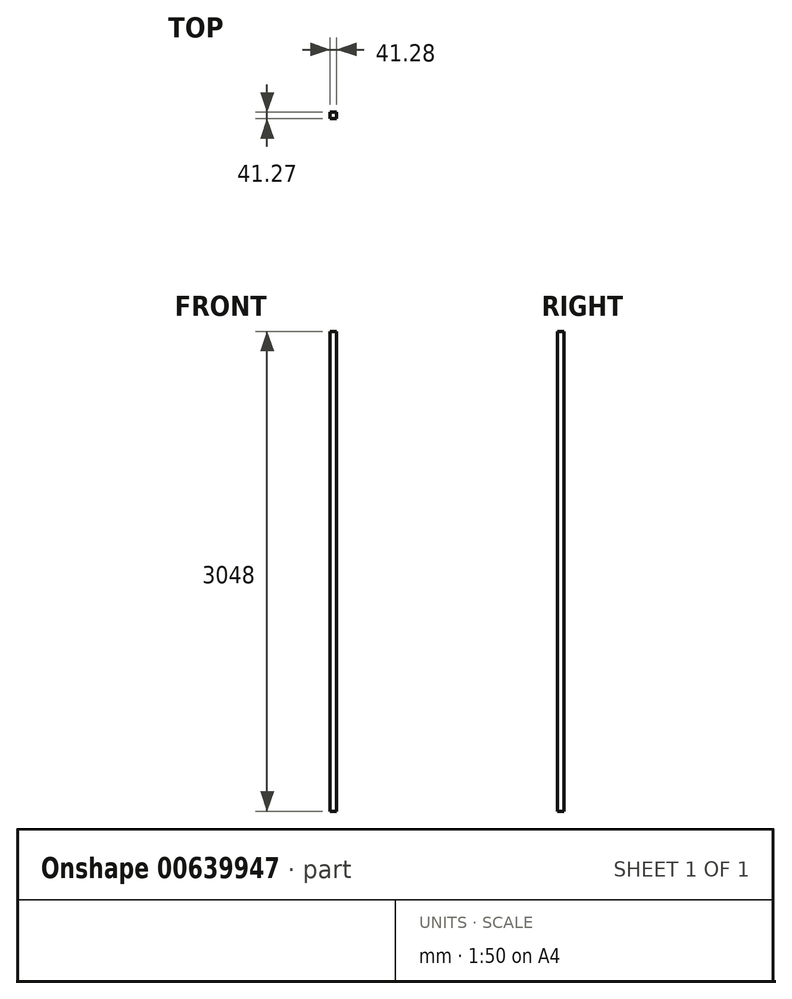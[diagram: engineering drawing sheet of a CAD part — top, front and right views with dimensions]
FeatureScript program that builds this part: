
annotation { "Feature Type Name" : "Feature", "Feature Type Description" : "" }
export const myFeature = defineFeature(function(context is Context, id is Id, definition is map)
    precondition{}
    {
        {
            var Q0;
            Q0=qCreatedBy(makeId("Front.planeOp"),FACE);
            var sketch = newSketch(context, id + "F0", { "sketchPlane" : qUnion([Q0])});
            skLineSegment(sketch, "E0.bottom", {"start": v(20.64, -1524) * mm, "end": v(-20.64, -1524) * mm});
            skLineSegment(sketch, "E0.top", {"start": v(20.64, 1524) * mm, "end": v(-20.64, 1524) * mm});
            skLineSegment(sketch, "E0.left", {"start": v(20.64, -1524) * mm, "end": v(20.64, 1524) * mm});
            skLineSegment(sketch, "E0.right", {"start": v(-20.64, -1524) * mm, "end": v(-20.64, 1524) * mm});
            skPoint(sketch, "E0.middle", {"position": v(0, 0) * mm});
            skSolve(sketch);
        }
        {
            var Q0;
            Q0=makeQuery(id+"F0.imprint","IMPRINT",FACE,{"disambiguationData":[TD([[makeQuery(id+"F0.imprint","IMPRINT",EDGE,{"derivedFrom":sQuery(id+"F0.wireOp",EDGE,"E0.bottom")}),-1.0]])]});
            extrude(context, id + "F1", {"entities" : qUnion([Q0]), "depth" : 41.27 * mm, "offsetDistance" : 25.4 * mm});
        }
    });
